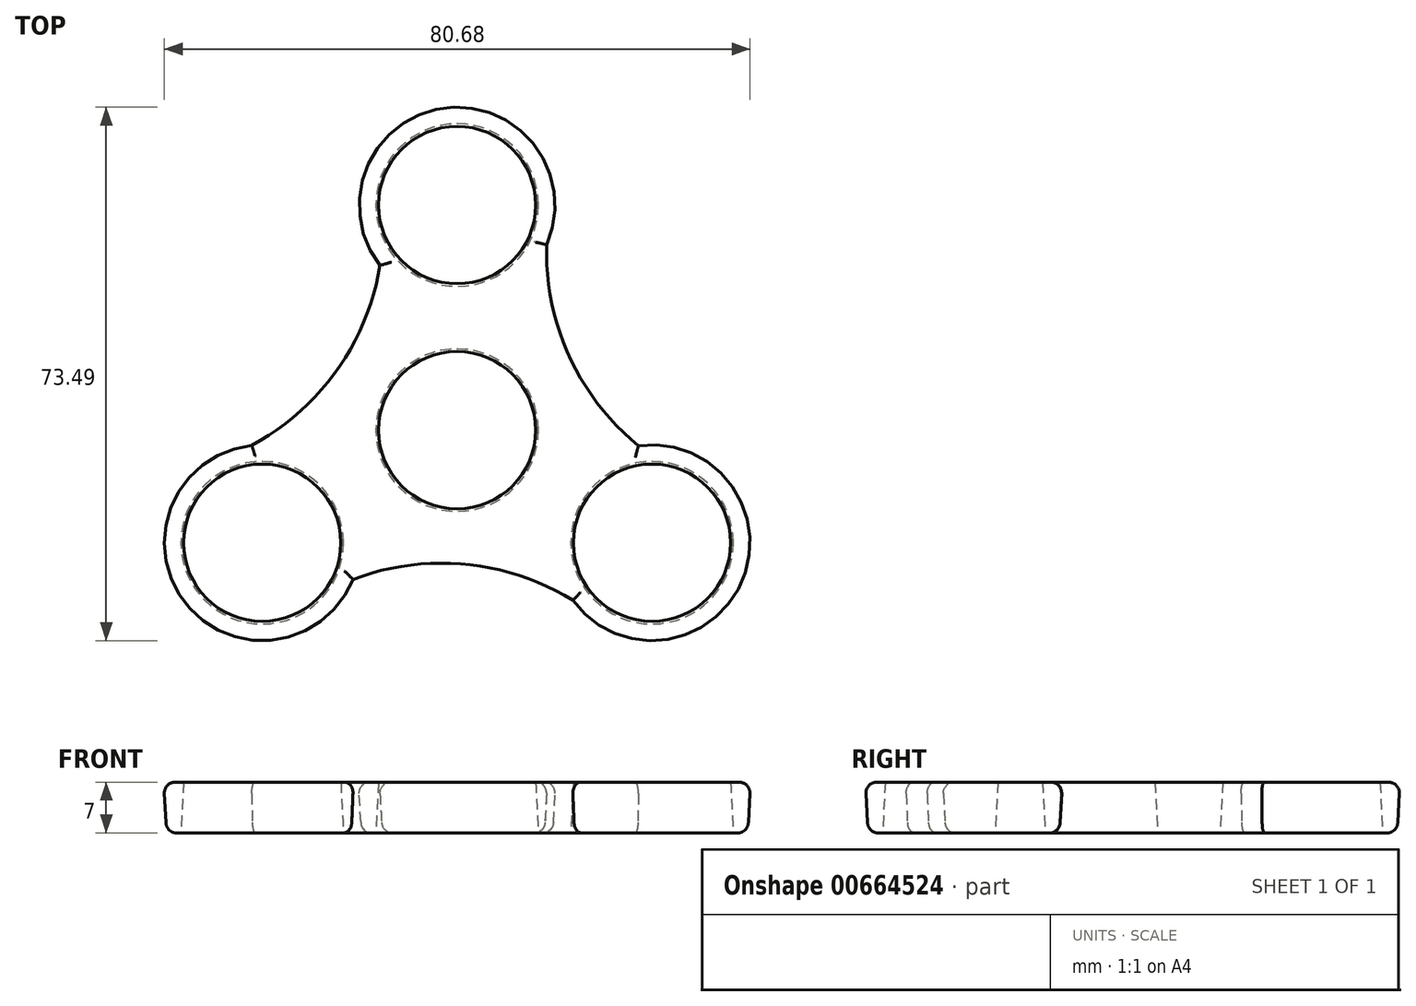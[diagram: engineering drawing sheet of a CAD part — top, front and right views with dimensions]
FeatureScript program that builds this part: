
annotation { "Feature Type Name" : "Feature", "Feature Type Description" : "" }
export const myFeature = defineFeature(function(context is Context, id is Id, definition is map)
    precondition{}
    {
        {
            var Q0;
            Q0=qCreatedBy(makeId("Top.planeOp"),FACE);
            var sketch = newSketch(context, id + "F0", { "sketchPlane" : qUnion([Q0])});
            skCircle(sketch, "E0", {"center": v(0, 0) * mm, "radius": 11.2 * mm});
            skCircle(sketch, "E1", {"center": v(0, 31.01) * mm, "radius": 11.2 * mm});
            skArc(sketch, "E2", {"start": v(12.05, 25.61) * mm, "mid": v(-1.65, 44.1) * mm, "end": v(-10.32, 22.79) * mm});
            skCircle(sketch, "E3.1.0", {"center": v(-26.86, -15.5) * mm, "radius": 11.2 * mm});
            skArc(sketch, "E3.1.1", {"start": v(-28.2, -2.37) * mm, "mid": v(-37.37, -23.49) * mm, "end": v(-14.57, -20.33) * mm});
            skCircle(sketch, "E3.2.0", {"center": v(26.86, -15.5) * mm, "radius": 11.2 * mm});
            skArc(sketch, "E3.2.1", {"start": v(16.16, -23.24) * mm, "mid": v(39.02, -20.62) * mm, "end": v(24.9, -2.45) * mm});
            skArc(sketch, "E4", {"start": v(12.05, 25.61) * mm, "mid": v(15.19, 10.08) * mm, "end": v(24.9, -2.45) * mm});
            skArc(sketch, "E5.1.0", {"start": v(-28.2, -2.37) * mm, "mid": v(-16.32, 8.12) * mm, "end": v(-10.32, 22.79) * mm});
            skArc(sketch, "E5.2.0", {"start": v(16.16, -23.24) * mm, "mid": v(1.13, -18.2) * mm, "end": v(-14.57, -20.33) * mm});
            skSolve(sketch);
        }
        {
            var Q0;
            Q0=makeQuery(id+"F0.imprint","IMPRINT",FACE,{"disambiguationData":[TD([[makeQuery(id+"F0.imprint","IMPRINT",EDGE,{"derivedFrom":sQuery(id+"F0.wireOp",EDGE,"E0")}),-1.0]])]});
            extrude(context, id + "F1", {"entities" : qUnion([Q0]), "depth" : 7 * mm, "offsetDistance" : 25 * mm, "hasDraft" : true, "draftAngle" : 3 * degree});
        }
        {
            var Q0;
            Q0=makeQuery(id+"F1.opExtrude","CAP_EDGE",EDGE,{"disambiguationData":[OSD([sQuery(id+"F0.wireOp",EDGE,"E5.1.0")])],"isStart":false});
            var Q1;
            Q1=makeQuery(id+"F1.opExtrude","CAP_EDGE",EDGE,{"disambiguationData":[OSD([sQuery(id+"F0.wireOp",EDGE,"E3.1.1")])],"isStart":false});
            var Q2;
            Q2=makeQuery(id+"F1.opExtrude","CAP_EDGE",EDGE,{"disambiguationData":[OSD([sQuery(id+"F0.wireOp",EDGE,"E5.2.0")])],"isStart":false});
            var Q3;
            Q3=makeQuery(id+"F1.opExtrude","CAP_EDGE",EDGE,{"disambiguationData":[OSD([sQuery(id+"F0.wireOp",EDGE,"E3.2.1")])],"isStart":false});
            var Q4;
            Q4=makeQuery(id+"F1.opExtrude","CAP_EDGE",EDGE,{"disambiguationData":[OSD([sQuery(id+"F0.wireOp",EDGE,"E2")])],"isStart":false});
            var Q5;
            Q5=makeQuery(id+"F1.opExtrude","CAP_EDGE",EDGE,{"disambiguationData":[OSD([sQuery(id+"F0.wireOp",EDGE,"E4")])],"isStart":false});
            fillet(context, id + "F2", {"entities" : qUnion([Q0, Q1, Q2, Q3, Q4, Q5]), "radius" : 1.5 * mm, "tangentPropagation" : true, "allowEdgeOverflow" : false});
        }
        {
            var Q0;
            Q0=makeQuery(id+"F1.opExtrude","CAP_EDGE",EDGE,{"disambiguationData":[OSD([sQuery(id+"F0.wireOp",EDGE,"E5.2.0")])],"isStart":true});
            var Q1;
            Q1=makeQuery(id+"F1.opExtrude","CAP_EDGE",EDGE,{"disambiguationData":[OSD([sQuery(id+"F0.wireOp",EDGE,"E3.1.1")])],"isStart":true});
            var Q2;
            Q2=makeQuery(id+"F1.opExtrude","CAP_EDGE",EDGE,{"disambiguationData":[OSD([sQuery(id+"F0.wireOp",EDGE,"E5.1.0")])],"isStart":true});
            var Q3;
            Q3=makeQuery(id+"F1.opExtrude","CAP_EDGE",EDGE,{"disambiguationData":[OSD([sQuery(id+"F0.wireOp",EDGE,"E2")])],"isStart":true});
            var Q4;
            Q4=makeQuery(id+"F1.opExtrude","CAP_EDGE",EDGE,{"disambiguationData":[OSD([sQuery(id+"F0.wireOp",EDGE,"E4")])],"isStart":true});
            var Q5;
            Q5=makeQuery(id+"F1.opExtrude","CAP_EDGE",EDGE,{"disambiguationData":[OSD([sQuery(id+"F0.wireOp",EDGE,"E3.2.1")])],"isStart":true});
            fillet(context, id + "F3", {"entities" : qUnion([Q0, Q1, Q2, Q3, Q4, Q5]), "radius" : 1.5 * mm, "tangentPropagation" : true, "allowEdgeOverflow" : false});
        }
    });
